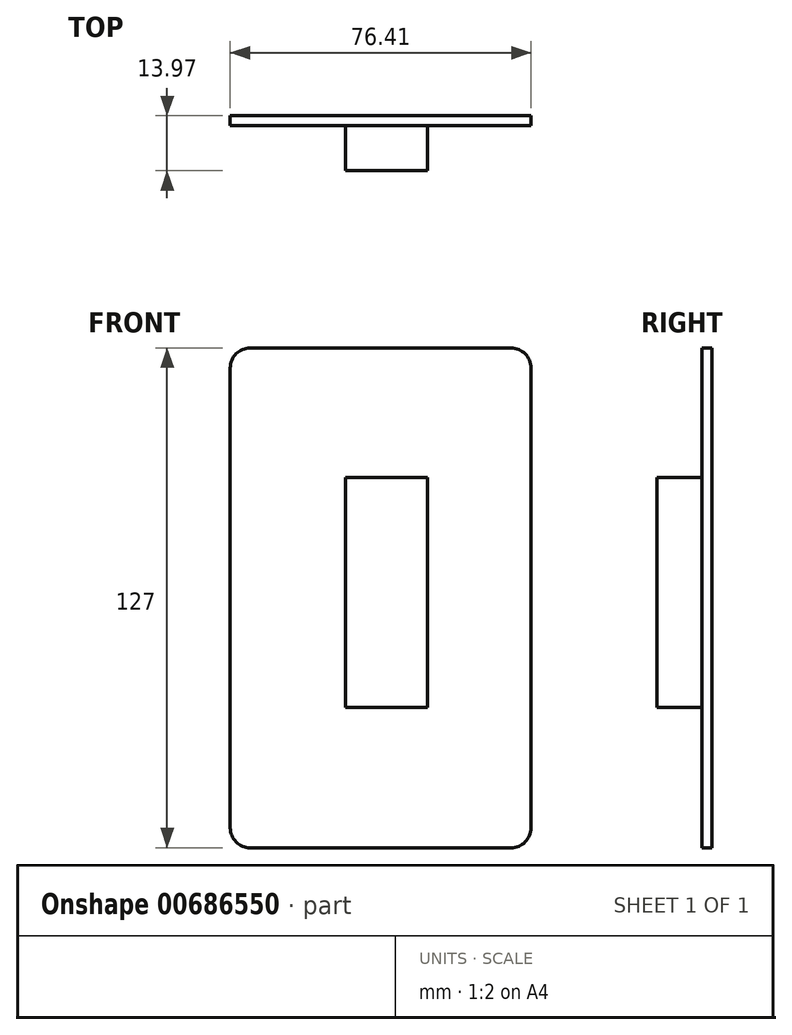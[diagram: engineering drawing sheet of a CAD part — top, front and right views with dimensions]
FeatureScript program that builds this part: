
annotation { "Feature Type Name" : "Feature", "Feature Type Description" : "" }
export const myFeature = defineFeature(function(context is Context, id is Id, definition is map)
    precondition{}
    {
        {
            var Q0;
            Q0=qCreatedBy(makeId("Front.planeOp"),FACE);
            var sketch = newSketch(context, id + "F0", { "sketchPlane" : qUnion([Q0])});
            skLineSegment(sketch, "E0", {"start": v(-40.28, 64.02) * mm, "end": v(36.13, 64.02) * mm});
            skLineSegment(sketch, "E1", {"start": v(36.13, 64.02) * mm, "end": v(36.13, -62.98) * mm});
            skLineSegment(sketch, "E2", {"start": v(36.13, -62.98) * mm, "end": v(-40.28, -62.98) * mm});
            skLineSegment(sketch, "E3", {"start": v(-40.28, -62.98) * mm, "end": v(-40.28, 64.02) * mm});
            skSolve(sketch);
        }
        {
            var Q0;
            Q0 = qSketchRegion(id + "F0", true);
            extrude(context, id + "F1", {"entities" : qUnion([Q0]), "depth" : 2.54 * mm, "offsetDistance" : 25.4 * mm});
        }
        {
            var Q0;
            Q0=makeQuery(id+"F1.opExtrude","SWEPT_EDGE",EDGE,{"disambiguationData":[OSD([sQuery(id+"F0.wireOp",EDGE,"E0"),sQuery(id+"F0.wireOp",EDGE,"E3")])]});
            var Q1;
            Q1=makeQuery(id+"F1.opExtrude","SWEPT_EDGE",EDGE,{"disambiguationData":[OSD([sQuery(id+"F0.wireOp",EDGE,"E0"),sQuery(id+"F0.wireOp",EDGE,"E1")])]});
            var Q2;
            Q2=makeQuery(id+"F1.opExtrude","SWEPT_EDGE",EDGE,{"disambiguationData":[OSD([sQuery(id+"F0.wireOp",EDGE,"E1"),sQuery(id+"F0.wireOp",EDGE,"E2")])]});
            var Q3;
            Q3=makeQuery(id+"F1.opExtrude","SWEPT_EDGE",EDGE,{"disambiguationData":[OSD([sQuery(id+"F0.wireOp",EDGE,"E2"),sQuery(id+"F0.wireOp",EDGE,"E3")])]});
            fillet(context, id + "F2", {"entities" : qUnion([Q0, Q1, Q2, Q3]), "radius" : 5.08 * mm, "tangentPropagation" : true, "allowEdgeOverflow" : false});
        }
        {
            var Q0;
            Q0=qCreatedBy(makeId("Front.planeOp"),FACE);
            var sketch = newSketch(context, id + "F3", { "sketchPlane" : qUnion([Q0])});
            skLineSegment(sketch, "E4", {"start": v(-10.94, 31.15) * mm, "end": v(-10.94, -27.27) * mm});
            skLineSegment(sketch, "E5", {"start": v(-10.94, -27.27) * mm, "end": v(9.83, -27.27) * mm});
            skLineSegment(sketch, "E6", {"start": v(9.83, -27.27) * mm, "end": v(9.83, 31.15) * mm});
            skLineSegment(sketch, "E7", {"start": v(9.83, 31.15) * mm, "end": v(-10.94, 31.15) * mm});
            skSolve(sketch);
        }
        {
            var Q0;
            Q0 = qSketchRegion(id + "F3", true);
            extrude(context, id + "F4", {"entities" : qUnion([Q0]), "operationType" : NewBodyOperationType.ADD, "depth" : 13.97 * mm, "offsetDistance" : 25.4 * mm});
        }
    });
